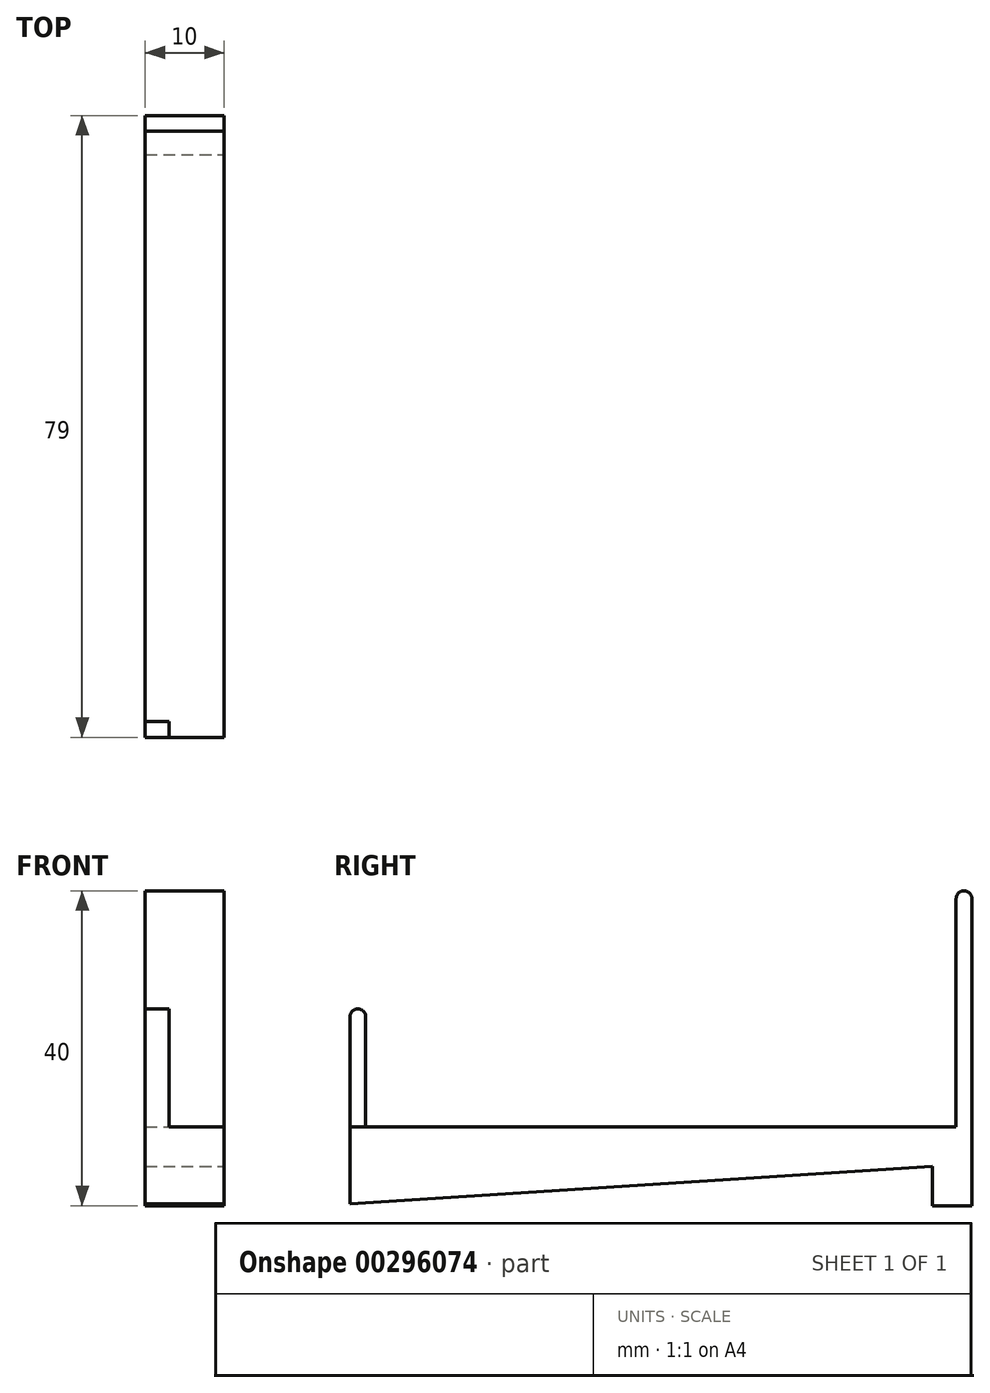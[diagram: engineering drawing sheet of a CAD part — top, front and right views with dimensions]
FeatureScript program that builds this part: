
annotation { "Feature Type Name" : "Feature", "Feature Type Description" : "" }
export const myFeature = defineFeature(function(context is Context, id is Id, definition is map)
    precondition{}
    {
        {
            var Q0;
            Q0=qCreatedBy(makeId("Top.planeOp"),FACE);
            var sketch = newSketch(context, id + "F0", { "sketchPlane" : qUnion([Q0])});
            skLineSegment(sketch, "E0.bottom", {"start": v(5, -39.5) * mm, "end": v(-5, -39.5) * mm});
            skLineSegment(sketch, "E0.top", {"start": v(5, 39.5) * mm, "end": v(-5, 39.5) * mm});
            skLineSegment(sketch, "E0.left", {"start": v(5, -39.5) * mm, "end": v(5, 39.5) * mm});
            skLineSegment(sketch, "E0.right", {"start": v(-5, -39.5) * mm, "end": v(-5, 39.5) * mm});
            skPoint(sketch, "E0.middle", {"position": v(0, 0) * mm});
            skSolve(sketch);
        }
        {
            var Q0;
            Q0 = qSketchRegion(id + "F0", true);
            extrude(context, id + "F1", {"entities" : qUnion([Q0]), "depth" : 10 * mm});
        }
        {
            var Q0;
            Q0=makeQuery(id+"F1.opExtrude","CAP_FACE",FACE,{"disambiguationData":[OSD([sQuery(id+"F0.wireOp",EDGE,"E0.bottom"),sQuery(id+"F0.wireOp",EDGE,"E0.top"),sQuery(id+"F0.wireOp",EDGE,"E0.left"),sQuery(id+"F0.wireOp",EDGE,"E0.right")])],"isStart":false});
            var sketch = newSketch(context, id + "F2", { "sketchPlane" : qUnion([Q0])});
            skLineSegment(sketch, "E1.bottom", {"start": v(-5, -39.5) * mm, "end": v(5, -39.5) * mm});
            skLineSegment(sketch, "E1.top", {"start": v(-5, -37.5) * mm, "end": v(5, -37.5) * mm});
            skLineSegment(sketch, "E1.left", {"start": v(-5, -39.5) * mm, "end": v(-5, -37.5) * mm});
            skLineSegment(sketch, "E1.right", {"start": v(5, -39.5) * mm, "end": v(5, -37.5) * mm});
            skSolve(sketch);
        }
        {
            var Q0;
            Q0 = qSketchRegion(id + "F2", true);
            extrude(context, id + "F3", {"entities" : qUnion([Q0]), "operationType" : NewBodyOperationType.ADD, "depth" : 15 * mm});
        }
        {
            var Q0;
            Q0=makeQuery(id+"F1.opExtrude","CAP_FACE",FACE,{"disambiguationData":[OSD([sQuery(id+"F0.wireOp",EDGE,"E0.bottom"),sQuery(id+"F0.wireOp",EDGE,"E0.top"),sQuery(id+"F0.wireOp",EDGE,"E0.left"),sQuery(id+"F0.wireOp",EDGE,"E0.right")])],"isStart":false});
            var sketch = newSketch(context, id + "F4", { "sketchPlane" : qUnion([Q0])});
            skLineSegment(sketch, "E2.bottom", {"start": v(-5, 39.5) * mm, "end": v(5, 39.5) * mm});
            skLineSegment(sketch, "E2.top", {"start": v(-5, 37.5) * mm, "end": v(5, 37.5) * mm});
            skLineSegment(sketch, "E2.left", {"start": v(-5, 39.5) * mm, "end": v(-5, 37.5) * mm});
            skLineSegment(sketch, "E2.right", {"start": v(5, 39.5) * mm, "end": v(5, 37.5) * mm});
            skSolve(sketch);
        }
        {
            var Q0;
            Q0 = qSketchRegion(id + "F4", true);
            extrude(context, id + "F5", {"entities" : qUnion([Q0]), "operationType" : NewBodyOperationType.ADD, "depth" : 30 * mm});
        }
        {
            var Q0;
            Q0=makeQuery(id+"F5.boolean.opBoolean","MERGE",FACE,{"derivedFrom":[makeQuery(id+"F3.boolean.opBoolean","MERGE",FACE,{"derivedFrom":[makeQuery(id+"F1.opExtrude","SWEPT_FACE",FACE,{"disambiguationData":[OSD([sQuery(id+"F0.wireOp",EDGE,"E0.left")])]}),makeQuery(id+"F3.opExtrude","SWEPT_FACE",FACE,{"disambiguationData":[OSD([sQuery(id+"F2.wireOp",EDGE,"E1.right")])]})]}),makeQuery(id+"F5.opExtrude","SWEPT_FACE",FACE,{"disambiguationData":[OSD([sQuery(id+"F4.wireOp",EDGE,"E2.right")])]})]});
            var sketch = newSketch(context, id + "F6", { "sketchPlane" : qUnion([Q0])});
            skLineSegment(sketch, "E3", {"start": v(-43.34, 0) * mm, "end": v(34.5, 5) * mm});
            skLineSegment(sketch, "E4", {"start": v(34.5, 5) * mm, "end": v(34.5, 0) * mm});
            skLineSegment(sketch, "E5", {"start": v(34.5, 0) * mm, "end": v(-43.34, 0) * mm});
            skSolve(sketch);
        }
        {
            var Q0;
            Q0 = qSketchRegion(id + "F6", true);
            extrude(context, id + "F7", {"entities" : qUnion([Q0]), "operationType" : NewBodyOperationType.REMOVE, "endBound" : BoundingType.THROUGH_ALL, "oppositeDirection" : true, "depth" : 25 * mm});
        }
        {
            var Q0;
            Q0=makeQuery(id+"F3.opExtrude","CAP_EDGE",EDGE,{"disambiguationData":[OSD([sQuery(id+"F2.wireOp",EDGE,"E1.bottom")])],"isStart":false});
            var Q1;
            Q1=makeQuery(id+"F3.opExtrude","CAP_EDGE",EDGE,{"disambiguationData":[OSD([sQuery(id+"F2.wireOp",EDGE,"E1.top")])],"isStart":false});
            var Q2;
            Q2=makeQuery(id+"F5.opExtrude","CAP_EDGE",EDGE,{"disambiguationData":[OSD([sQuery(id+"F4.wireOp",EDGE,"E2.top")])],"isStart":false});
            var Q3;
            Q3=makeQuery(id+"F5.opExtrude","CAP_EDGE",EDGE,{"disambiguationData":[OSD([sQuery(id+"F4.wireOp",EDGE,"E2.bottom")])],"isStart":false});
            var Q4;
            Q4=makeQuery(id+"F3.opExtrude","CAP_EDGE",EDGE,{"disambiguationData":[OSD([sQuery(id+"F2.wireOp",EDGE,"E1.top")])],"isStart":true});
            var Q5;
            Q5=makeQuery(id+"F5.opExtrude","CAP_EDGE",EDGE,{"disambiguationData":[OSD([sQuery(id+"F4.wireOp",EDGE,"E2.top")])],"isStart":true});
            fillet(context, id + "F8", {"entities" : qUnion([Q0, Q1, Q2, Q3, Q4, Q5]), "radius" : 1 * mm, "tangentPropagation" : true, "allowEdgeOverflow" : false});
        }
        {
            var Q0;
            Q0=makeQuery(id+"F5.boolean.opBoolean","MERGE",FACE,{"derivedFrom":[makeQuery(id+"F3.boolean.opBoolean","MERGE",FACE,{"derivedFrom":[makeQuery(id+"F1.opExtrude","SWEPT_FACE",FACE,{"disambiguationData":[OSD([sQuery(id+"F0.wireOp",EDGE,"E0.left")])]}),makeQuery(id+"F3.opExtrude","SWEPT_FACE",FACE,{"disambiguationData":[OSD([sQuery(id+"F2.wireOp",EDGE,"E1.right")])]})]}),makeQuery(id+"F5.opExtrude","SWEPT_FACE",FACE,{"disambiguationData":[OSD([sQuery(id+"F4.wireOp",EDGE,"E2.right")])]})]});
            var sketch = newSketch(context, id + "F9", { "sketchPlane" : qUnion([Q0])});
            skLineSegment(sketch, "E6.bottom", {"start": v(-39.5, 25) * mm, "end": v(-34.58, 25) * mm});
            skLineSegment(sketch, "E6.top", {"start": v(-39.5, 10) * mm, "end": v(-34.58, 10) * mm});
            skLineSegment(sketch, "E6.left", {"start": v(-39.5, 25) * mm, "end": v(-39.5, 10) * mm});
            skLineSegment(sketch, "E6.right", {"start": v(-34.58, 25) * mm, "end": v(-34.58, 10) * mm});
            skSolve(sketch);
        }
        {
            var Q0;
            Q0 = qSketchRegion(id + "F9", true);
            extrude(context, id + "F10", {"entities" : qUnion([Q0]), "operationType" : NewBodyOperationType.REMOVE, "oppositeDirection" : true, "depth" : 7 * mm});
        }
    });
